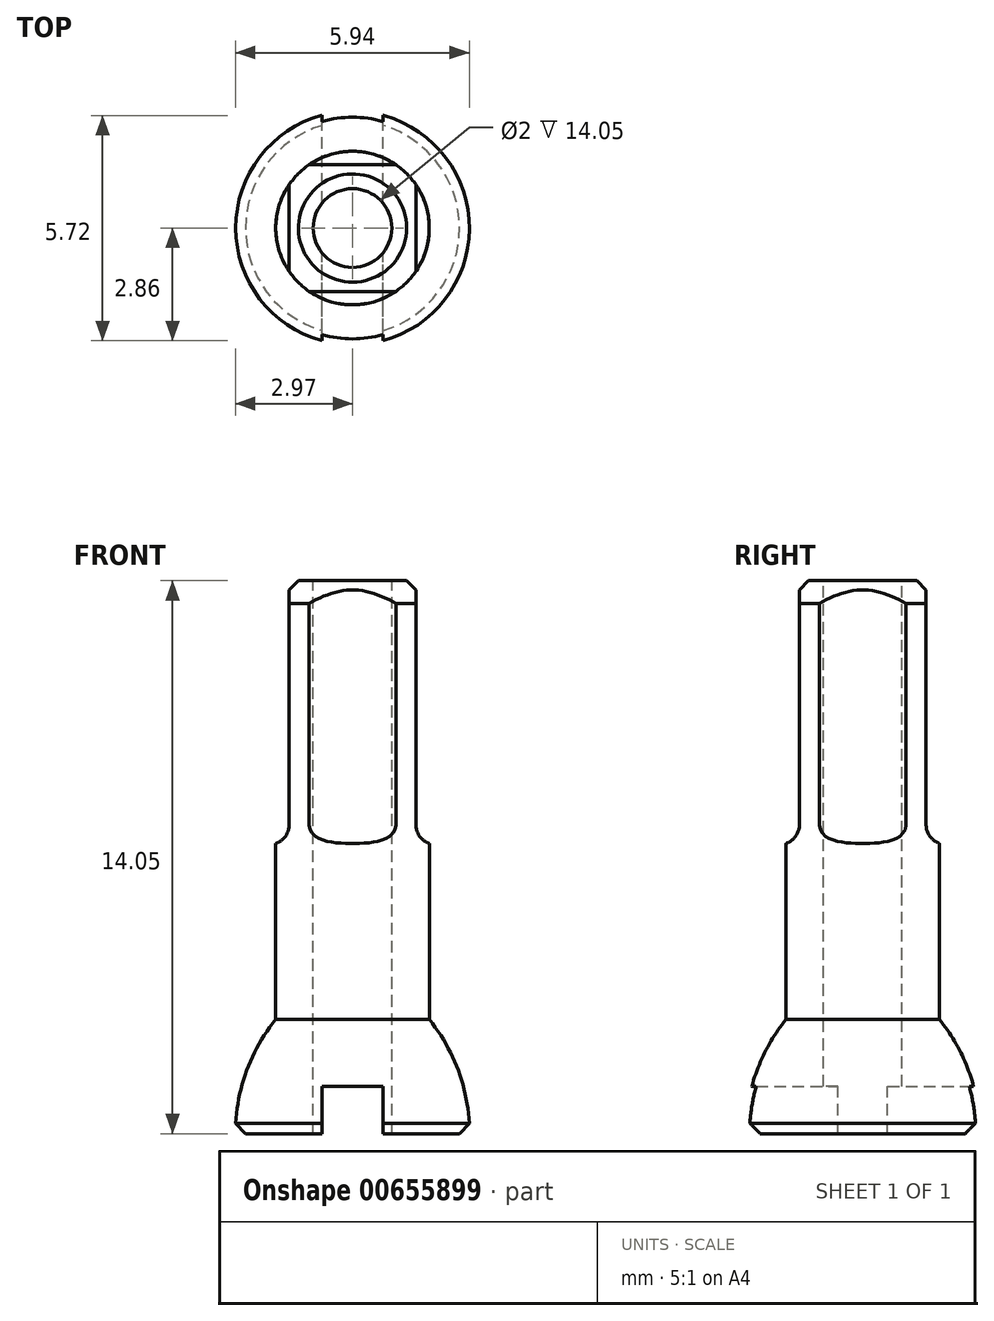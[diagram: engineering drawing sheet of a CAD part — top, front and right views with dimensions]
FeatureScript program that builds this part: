
annotation { "Feature Type Name" : "Feature", "Feature Type Description" : "" }
export const myFeature = defineFeature(function(context is Context, id is Id, definition is map)
    precondition{}
    {
        {
            var Q0;
            Q0=qCreatedBy(makeId("Right.planeOp"),FACE);
            var sketch = newSketch(context, id + "F0", { "sketchPlane" : qUnion([Q0])});
            skLineSegment(sketch, "E0", {"start": v(0, 0) * mm, "end": v(0, 15.52) * mm, "construction": true});
            skLineSegment(sketch, "E1", {"start": v(0, 0) * mm, "end": v(2.98, 0) * mm});
            skLineSegment(sketch, "E2", {"start": v(1.95, 2.9) * mm, "end": v(1.95, 14.05) * mm});
            skLineSegment(sketch, "E3", {"start": v(1.95, 14.05) * mm, "end": v(0, 14.05) * mm});
            skLineSegment(sketch, "E4", {"start": v(0, 14.05) * mm, "end": v(0, 0) * mm});
            skArc(sketch, "E5", {"start": v(2.98, 0) * mm, "mid": v(2.71, 1.54) * mm, "end": v(1.95, 2.9) * mm});
            skSolve(sketch);
        }
        {
            var Q0;
            Q0 = qSketchRegion(id + "F0", true);
            var Q1;
            Q1=sQuery(id+"F0.wireOp",EDGE,"E0");
            revolve(context, id + "F1", {"entities" : qUnion([Q0]), "axis" : qUnion([Q1]), "revolveType" : RevolveType.FULL});
        }
        {
            var Q0;
            Q0=makeQuery(id+"F1.opRevolve","SWEPT_FACE",FACE,{"disambiguationData":[OSD([sQuery(id+"F0.wireOp",EDGE,"E3")])]});
            var sketch = newSketch(context, id + "F2", { "sketchPlane" : qUnion([Q0])});
            skLineSegment(sketch, "E6.bottom", {"start": v(1.6, 1.61) * mm, "end": v(-1.61, 1.61) * mm});
            skLineSegment(sketch, "E6.top", {"start": v(1.6, -1.6) * mm, "end": v(-1.61, -1.6) * mm});
            skLineSegment(sketch, "E6.left", {"start": v(1.61, 1.61) * mm, "end": v(1.6, -1.6) * mm});
            skLineSegment(sketch, "E6.right", {"start": v(-1.61, 1.61) * mm, "end": v(-1.61, -1.6) * mm});
            skPoint(sketch, "E6.middle", {"position": v(0, 0) * mm});
            skCircle(sketch, "E7", {"center": v(0, 0) * mm, "radius": 7.5 * mm});
            skSolve(sketch);
        }
        {
            var Q0;
            Q0 = qSketchRegion(id + "F2", true);
            extrude(context, id + "F3", {"entities" : qUnion([Q0]), "operationType" : NewBodyOperationType.REMOVE, "oppositeDirection" : true, "depth" : 6.7 * mm, "offsetDistance" : 25 * mm});
        }
        {
            var Q0;
            Q0=makeQuery(id+"F3.boolean.opBoolean","COPY",EDGE,{"derivedFrom":makeQuery(id+"F3.opExtrude","CAP_EDGE",EDGE,{"disambiguationData":[OSD([sQuery(id+"F2.wireOp",EDGE,"E6.left")])],"isStart":false})});
            var Q1;
            Q1=makeQuery(id+"F3.boolean.opBoolean","COPY",EDGE,{"derivedFrom":makeQuery(id+"F3.opExtrude","CAP_EDGE",EDGE,{"disambiguationData":[OSD([sQuery(id+"F2.wireOp",EDGE,"E6.top")])],"isStart":false})});
            var Q2;
            Q2=makeQuery(id+"F3.boolean.opBoolean","COPY",EDGE,{"derivedFrom":makeQuery(id+"F3.opExtrude","CAP_EDGE",EDGE,{"disambiguationData":[OSD([sQuery(id+"F2.wireOp",EDGE,"E6.bottom")])],"isStart":false})});
            var Q3;
            Q3=makeQuery(id+"F3.boolean.opBoolean","COPY",EDGE,{"derivedFrom":makeQuery(id+"F3.opExtrude","CAP_EDGE",EDGE,{"disambiguationData":[OSD([sQuery(id+"F2.wireOp",EDGE,"E6.right")])],"isStart":false})});
            fillet(context, id + "F4", {"entities" : qUnion([Q0, Q1, Q2, Q3]), "radius" : 0.5 * mm, "tangentPropagation" : true, "allowEdgeOverflow" : false});
        }
        {
            var Q0;
            Q0=makeQuery(id+"F1.opRevolve","SWEPT_EDGE",EDGE,{"disambiguationData":[OSD([sQuery(id+"F0.wireOp",EDGE,"E1"),sQuery(id+"F0.wireOp",EDGE,"E5")])]});
            chamfer(context, id + "F5", {"entities" : qUnion([Q0]), "width" : 0.25 * mm, "tangentPropagation" : true});
        }
        {
            var Q0;
            Q0=makeQuery(id+"F1.opRevolve","SWEPT_FACE",FACE,{"disambiguationData":[OSD([sQuery(id+"F0.wireOp",EDGE,"E3")])]});
            var sketch = newSketch(context, id + "F6", { "sketchPlane" : qUnion([Q0])});
            skCircle(sketch, "E8", {"center": v(0, 0) * mm, "radius": 1 * mm});
            skSolve(sketch);
        }
        {
            var Q0;
            Q0 = qSketchRegion(id + "F6", true);
            extrude(context, id + "F7", {"entities" : qUnion([Q0]), "operationType" : NewBodyOperationType.REMOVE, "endBound" : BoundingType.THROUGH_ALL, "oppositeDirection" : true, "depth" : 25 * mm, "offsetDistance" : 25 * mm});
        }
        {
            var Q0;
            Q0=qCreatedBy(makeId("Front.planeOp"),FACE);
            var sketch = newSketch(context, id + "F8", { "sketchPlane" : qUnion([Q0])});
            skLineSegment(sketch, "E9", {"start": v(-1.38, 14.05) * mm, "end": v(-3.37, 12.05) * mm});
            skLineSegment(sketch, "E10", {"start": v(-3.37, 12.05) * mm, "end": v(-3.37, 14.05) * mm});
            skLineSegment(sketch, "E11", {"start": v(-3.37, 14.05) * mm, "end": v(-1.38, 14.05) * mm});
            skLineSegment(sketch, "E12", {"start": v(0, 0) * mm, "end": v(0, 19.8) * mm, "construction": true});
            skSolve(sketch);
        }
        {
            var Q0;
            Q0 = qSketchRegion(id + "F8", true);
            var Q1;
            Q1=sQuery(id+"F8.wireOp",EDGE,"E12");
            revolve(context, id + "F9", {"operationType" : NewBodyOperationType.REMOVE, "entities" : qUnion([Q0]), "axis" : qUnion([Q1]), "revolveType" : RevolveType.FULL, "oppositeDirection" : true});
        }
        {
            var Q0;
            Q0=makeQuery(id+"F1.opRevolve","SWEPT_FACE",FACE,{"disambiguationData":[OSD([sQuery(id+"F0.wireOp",EDGE,"E1")])]});
            var sketch = newSketch(context, id + "F10", { "sketchPlane" : qUnion([Q0])});
            skLineSegment(sketch, "E13.bottom", {"start": v(0.77, 5) * mm, "end": v(-0.78, 5) * mm});
            skLineSegment(sketch, "E13.top", {"start": v(0.78, -5) * mm, "end": v(-0.77, -5) * mm});
            skLineSegment(sketch, "E13.left", {"start": v(0.77, 5) * mm, "end": v(0.78, -5) * mm});
            skLineSegment(sketch, "E13.right", {"start": v(-0.78, 5) * mm, "end": v(-0.77, -5) * mm});
            skPoint(sketch, "E13.middle", {"position": v(0, 0) * mm});
            skSolve(sketch);
        }
        {
            var Q0;
            Q0 = qSketchRegion(id + "F10", true);
            extrude(context, id + "F11", {"entities" : qUnion([Q0]), "operationType" : NewBodyOperationType.REMOVE, "oppositeDirection" : true, "depth" : 1.2 * mm, "offsetDistance" : 25 * mm});
        }
    });
